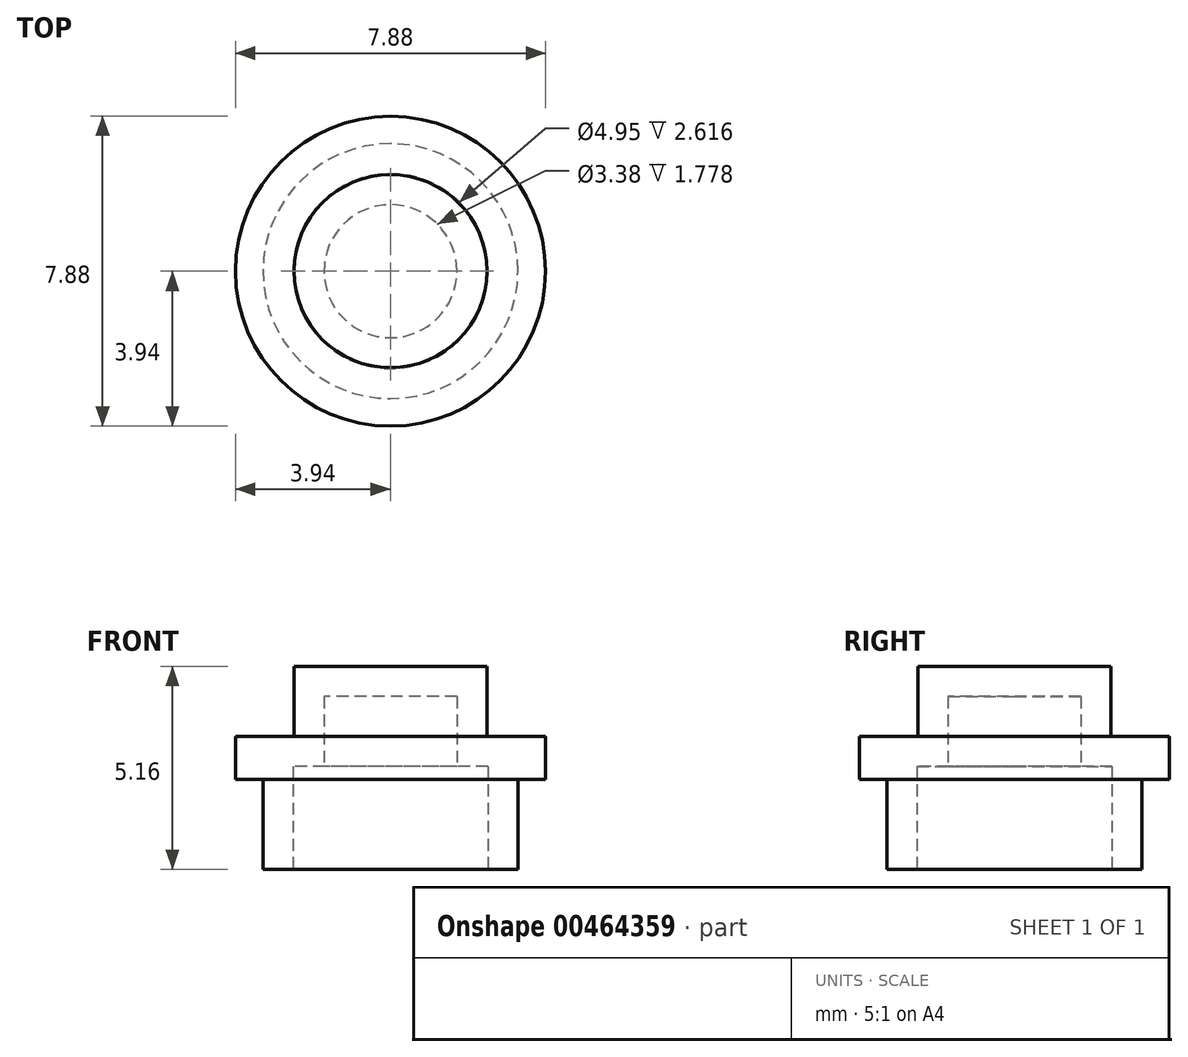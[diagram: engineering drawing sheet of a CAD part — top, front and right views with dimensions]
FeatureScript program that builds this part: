
annotation { "Feature Type Name" : "Feature", "Feature Type Description" : "" }
export const myFeature = defineFeature(function(context is Context, id is Id, definition is map)
    precondition{}
    {
        {
            var Q0;
            Q0=qCreatedBy(makeId("Top.planeOp"),FACE);
            var sketch = newSketch(context, id + "F0", { "sketchPlane" : qUnion([Q0])});
            skCircle(sketch, "E0", {"center": v(0, 0) * mm, "radius": 3.24 * mm});
            skSolve(sketch);
        }
        {
            var Q0;
            Q0=qSketchRegion(id+"F0",true);
            extrude(context, id + "F1", {"entities" : qUnion([Q0]), "depth" : 2.3 * mm});
        }
        {
            var Q0;
            Q0=makeQuery(id+"F1.opExtrude","CAP_FACE",FACE,{"disambiguationData":[OSD([sQuery(id+"F0.wireOp",EDGE,"E0")])],"isStart":false});
            var sketch = newSketch(context, id + "F2", { "sketchPlane" : qUnion([Q0])});
            skCircle(sketch, "E1", {"center": v(0, 0) * mm, "radius": 3.94 * mm});
            skSolve(sketch);
        }
        {
            var Q0;
            Q0=qSketchRegion(id+"F2",true);
            extrude(context, id + "F3", {"entities" : qUnion([Q0]), "operationType" : NewBodyOperationType.ADD, "depth" : 1.1 * mm});
        }
        {
            var Q0;
            Q0=makeQuery(id+"F3.opExtrude","CAP_FACE",FACE,{"disambiguationData":[OSD([sQuery(id+"F2.wireOp",EDGE,"E1")])],"isStart":false});
            var sketch = newSketch(context, id + "F4", { "sketchPlane" : qUnion([Q0])});
            skCircle(sketch, "E2", {"center": v(0, 0) * mm, "radius": 2.45 * mm});
            skSolve(sketch);
        }
        {
            var Q0;
            Q0=qSketchRegion(id+"F4",true);
            extrude(context, id + "F5", {"entities" : qUnion([Q0]), "operationType" : NewBodyOperationType.ADD, "depth" : 1.78 * mm});
        }
        {
            var Q0;
            Q0=makeQuery(id+"F1.opExtrude","CAP_FACE",FACE,{"disambiguationData":[OSD([sQuery(id+"F0.wireOp",EDGE,"E0")])],"isStart":true});
            shell(context, id + "F6", {"entities" : qUnion([Q0]), "thickness" : 0.76 * mm});
        }
    });
